# Revit family: Deca_Bide 3 furos_Vogue Plus_B.5
name_source: partatom
category: Plumbing Fixtures
units: mm (PartAtom-declared; Revit-internal decimal feet)

## family parameters
Cut with Voids When Loaded = No
Host = Face
Part Type = Normal
Room Calculation Point = No
Round Connector Dimension = Use Radius
Shared = No

## types (1)
- B.5.17_Branco
    Acompanha o Produto = -
    Aprovado por = quattroD
    Atendimento ao Cliente = 0800-0117073
    CWFU = 0
    Categoria = BACIAS E BIDES
    Composição Anel Vedação = -
    Composição Assento = -
    Composição Básica = Argila, feldspato, caulim, vidrados e corantes inorgânicos.
    Composição Componente = Não Possui
    Consumo = -
    Cor Interna = -
    Cor Principal = Branco
    Cor Secundária = -
    Cores Componente = Não Possui
    Criado por = quattroD
    Código Pai = B.5
    Default Elevation = 0 mm  [stored 0 ft]
    Description = Bidê com 3 furos
    Diâmetro Ponto de Esgoto = 40 mm  [stored 0.131234 ft]
    Diâmetro Água Fria = 15 mm  [stored 0.0492126 ft]
    Diâmetro Água Quente = 15 mm  [stored 0.0492126 ft]
    Informações Complementares = -
    Itens de Instalação = 1895.C14; 1895.C26; 1895.C33; 1895.C34; 1895.C35; 1895.C37; 1895.C38; 1895.C40.CR; 1895.C43; 1895.C50; 1895.C52; 1895.C64; 1895.C81; 1895.C84; 1895.C86; 1895.C87; 1895.C90; 1895.C94; SP.121.01
    Linha = Vogue Plus
    Manufacturer = Deca
    Material = Deca_Branco
    Model = B.5.17
    Norma = NBR-16728-1;NBR-16728-2
    Peso Líquido (Kg) = 19.207
    Pressão máx. funcionamento = -
    Pressão mín. Aquec. Acúmulo = -
    Pressão mín. Aquec. Passagem = -
    Pressão mín. funcionamento = -
    Raio Ponto de Esgoto = 20 mm
    Raio Água Fria = 8 mm  [stored 0.0262467 ft]
    Raio Água Quente = 8 mm  [stored 0.0262467 ft]
    Saída de Esgoto = Saída de Esgoto Vertical
    Segmento = Banheiro Médio
    Tipo de dispositivo economizador = -
    Tipo de mecanismo utilizado = -
    Tipo de rosca de entrada = -
    Tipo de rosca de saída = -
    URL = www.deca.com.br
    Vazão na Pressão máx. (L/min) = -
    Vazão na Pressão mín. (L/min) = -
    WFU = 0

note: [stored X ft] marks values corroborated as IEEE doubles in the binary element streams (Revit-internal decimal feet)

## geometry (parser evidence)
native form markers: Sweep x1
no freeform markers — native parametric forms only
